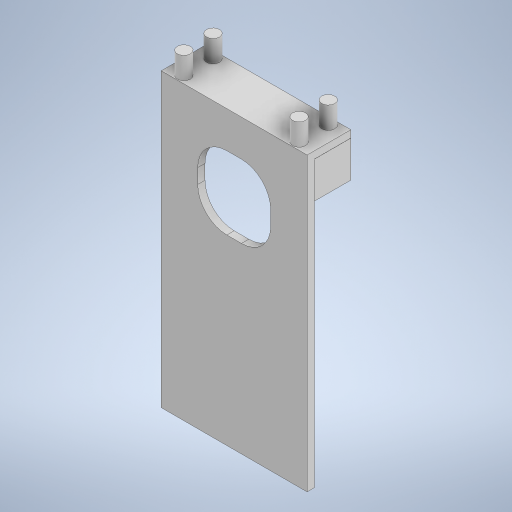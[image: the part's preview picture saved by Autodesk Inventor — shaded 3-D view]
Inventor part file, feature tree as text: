
AUTODESK INVENTOR PART (.ipt)
format: ipt  version: 2023 (Build 270158000, 158)  size: 312,832 bytes
history: native  units: mm
features: extrude x7, sketch x7
ambient origin geometry x8: Origin, YZ Plane, XZ Plane, XY Plane, X Axis, Y Axis, Z Axis, Center Point
bodies: Solid1 (feature_tree)
feature tree (14):
  extrude  "Extrusion1"  Depth=200.0mm
  extrude  "Extrusion6"  Depth=50.0mm
  sketch  "Sketch15"  dims[d22=50.0mm d23=20.0mm]
  sketch  "Sketch16"  dims[d24=5.0mm d25=0.0mm d46=100.0mm]
  extrude  "Extrusion11"  Depth=20.0mm
  extrude  "Extrusion12"  Depth=100.0mm
  extrude  "Extrusion13"  Depth=30.0mm
  extrude  "Extrusion14"  Depth=9.0mm
  extrude  "Extrusion16"  Depth=5.0mm TaperAngle=0.0deg
  sketch  "Sketch1"  dims[d0=100.0mm d1=200.0mm]
  sketch  "Sketch6"  dims[d2=5.0mm d3=0.0mm d21=50.0mm]
  sketch  "Sketch17"  dims[d47=30.0mm d48=9.0mm]
  sketch  "Sketch18"  dims[d49=9.0mm d50=9.0mm]
  sketch  "Sketch20"  dims[d51=9.0mm d52=5.0mm d53=0.0mm d54=15.0mm d55=0.0mm d56=100.0mm d57=30.0mm d58=5.0mm d59=0.0mm d60=5.0mm d61=0.0mm d64=5.0mm d65=0.0mm]
